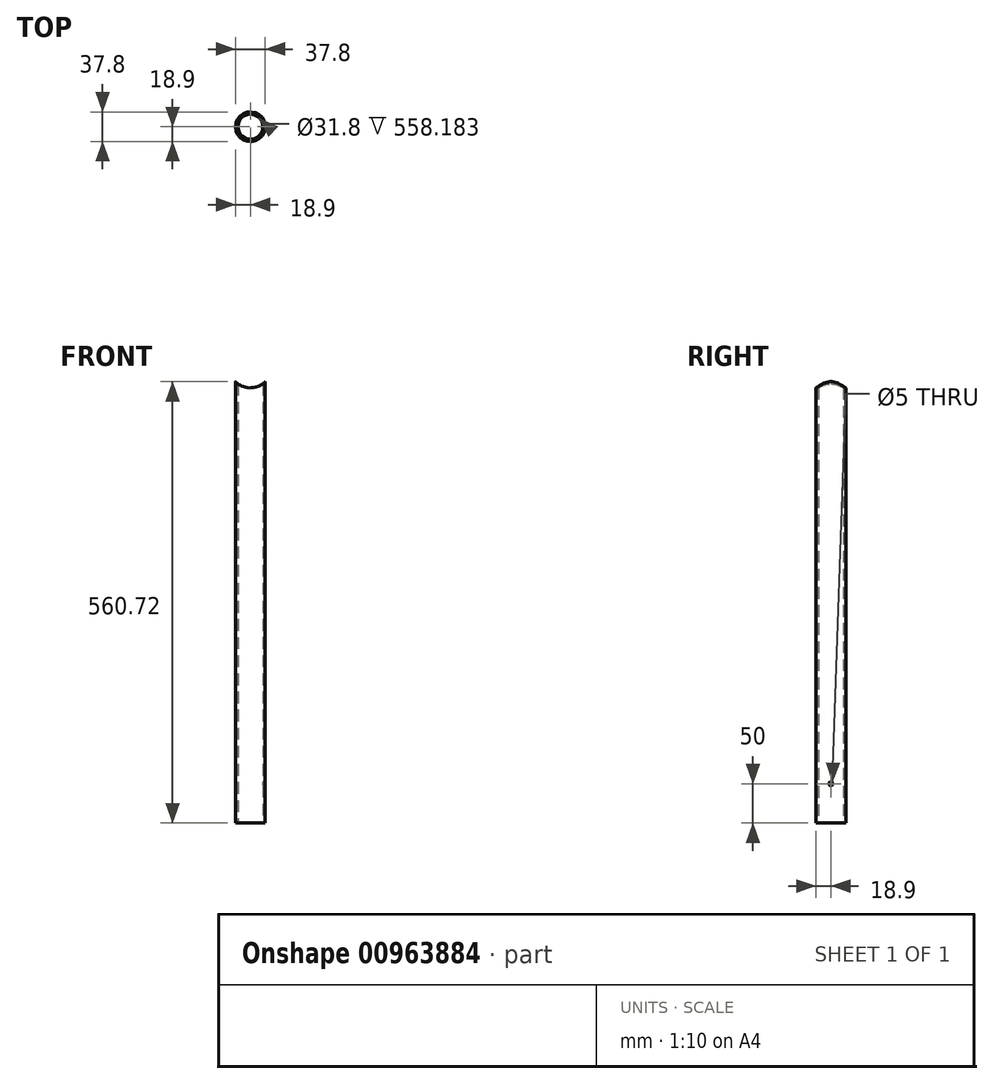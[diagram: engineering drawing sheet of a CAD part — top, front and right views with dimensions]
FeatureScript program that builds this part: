
annotation { "Feature Type Name" : "Feature", "Feature Type Description" : "" }
export const myFeature = defineFeature(function(context is Context, id is Id, definition is map)
    precondition{}
    {
        {
            var Q0;
            Q0=qCreatedBy(makeId("Top.planeOp"),FACE);
            var sketch = newSketch(context, id + "F0", { "sketchPlane" : qUnion([Q0])});
            skCircle(sketch, "E0", {"center": v(0, 0) * mm, "radius": 15.9 * mm});
            skCircle(sketch, "E1", {"center": v(0, 0) * mm, "radius": 18.9 * mm});
            skSolve(sketch);
        }
        {
            var Q0;
            Q0=makeQuery(id+"F0.imprint","IMPRINT",FACE,{"disambiguationData":[TD([[makeQuery(id+"F0.imprint","IMPRINT",EDGE,{"derivedFrom":sQuery(id+"F0.wireOp",EDGE,"E0")}),-1.0]])]});
            extrude(context, id + "F1", {"entities" : qUnion([Q0]), "depth" : 580 * mm, "offsetDistance" : 25 * mm});
        }
        {
            var Q0;
            Q0=qCreatedBy(makeId("Front.planeOp"),FACE);
            var sketch = newSketch(context, id + "F2", { "sketchPlane" : qUnion([Q0])});
            skLineSegment(sketch, "E2", {"start": v(0, 0) * mm, "end": v(0, 794.75) * mm, "construction": true});
            skSolve(sketch);
        }
        {
            var Q0;
            Q0=makeQuery(id+"F1.opExtrude","CAP_FACE",FACE,{"disambiguationData":[OSD([sQuery(id+"F0.wireOp",EDGE,"E0"),sQuery(id+"F0.wireOp",EDGE,"E1")])],"isStart":false});
            var sketch = newSketch(context, id + "F3", { "sketchPlane" : qUnion([Q0])});
            skLineSegment(sketch, "E3", {"start": v(0, -41.78) * mm, "end": v(0, 40.35) * mm, "construction": true});
            skLineSegment(sketch, "E4", {"start": v(-49.62, 0) * mm, "end": v(46.23, 0) * mm, "construction": true});
            skSolve(sketch);
        }
        {
            var Q0;
            Q0=sQuery(id+"F3.wireOp",EDGE,"E4");
            var Q1;
            Q1=sQuery(id+"F3.wireOp",EDGE,"E3");
            cPlane(context, id + "F4", {"entities" : qUnion([Q0, Q1]), "cplaneType" : CPlaneType.LINE_ANGLE, "offset" : 25 * mm, "angle" : 90 * degree, "width" : 150 * mm, "height" : 150 * mm});
        }
        {
            var Q0;
            Q0=qCreatedBy(id+"F4.planeOp",FACE);
            var sketch = newSketch(context, id + "F5", { "sketchPlane" : qUnion([Q0])});
            skCircle(sketch, "E5", {"center": v(0, 580) * mm, "radius": 27 * mm});
            skSolve(sketch);
        }
        {
            var Q0;
            Q0=makeQuery(id+"F5.imprint","IMPRINT",FACE,{"disambiguationData":[TD([[makeQuery(id+"F5.imprint","IMPRINT",EDGE,{"derivedFrom":sQuery(id+"F5.wireOp",EDGE,"E5")}),1.0]])]});
            extrude(context, id + "F6", {"entities" : qUnion([Q0]), "operationType" : NewBodyOperationType.REMOVE, "endBound" : BoundingType.SYMMETRIC, "oppositeDirection" : true, "depth" : 100 * mm, "offsetDistance" : 25 * mm});
        }
        {
            var Q0;
            Q0=qCreatedBy(makeId("Right.planeOp"),FACE);
            var sketch = newSketch(context, id + "F7", { "sketchPlane" : qUnion([Q0])});
            skLineSegment(sketch, "E6", {"start": v(0, -28.3) * mm, "end": v(0, 104.28) * mm, "construction": true});
            skCircle(sketch, "E7", {"center": v(0, 50) * mm, "radius": 2.5 * mm});
            skSolve(sketch);
        }
        {
            var Q0;
            Q0 = qSketchRegion(id + "F7", true);
            extrude(context, id + "F8", {"entities" : qUnion([Q0]), "operationType" : NewBodyOperationType.REMOVE, "endBound" : BoundingType.THROUGH_ALL, "depth" : 25 * mm, "offsetDistance" : 25 * mm});
        }
    });
